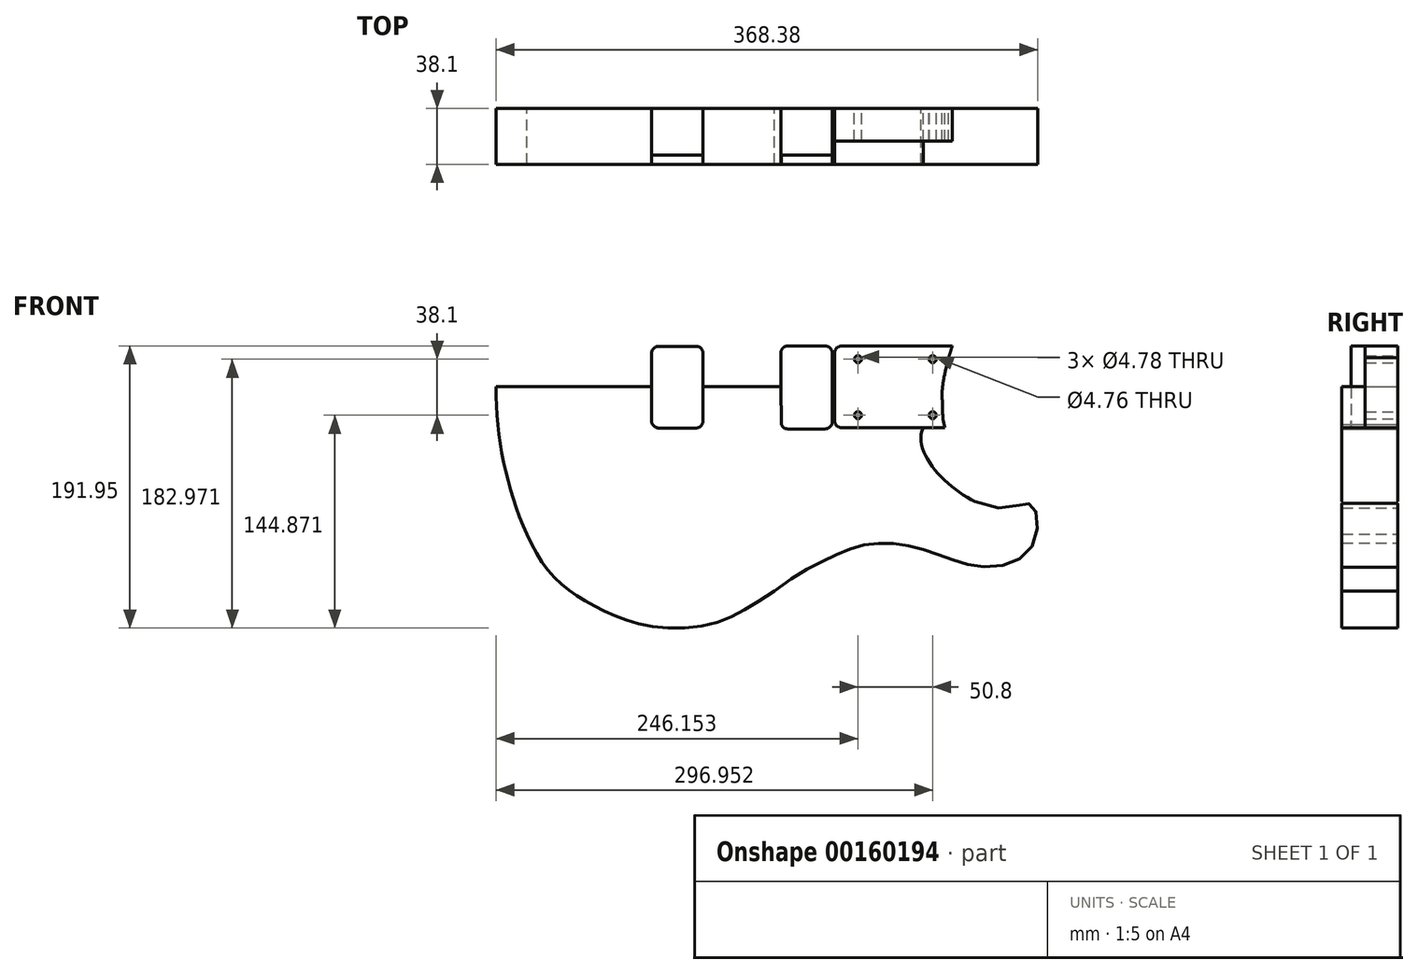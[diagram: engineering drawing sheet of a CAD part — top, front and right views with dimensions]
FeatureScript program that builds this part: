
annotation { "Feature Type Name" : "Feature", "Feature Type Description" : "" }
export const myFeature = defineFeature(function(context is Context, id is Id, definition is map)
    precondition{}
    {
        {
            var Q0;
            Q0=qCreatedBy(makeId("Front.planeOp"),FACE);
            var sketch = newSketch(context, id + "F0", { "sketchPlane" : qUnion([Q0])});
            skLineSegment(sketch, "E0", {"start": v(-152.4, 0) * mm, "end": v(0, 0) * mm});
            skLineSegment(sketch, "E1", {"start": v(0, 0) * mm, "end": v(196.6, 0) * mm});
            skLineSegment(sketch, "E2", {"start": v(0, 0) * mm, "end": v(0, 152.4) * mm});
            skLineSegment(sketch, "E3", {"start": v(0, 152.4) * mm, "end": v(0, 0) * mm});
            skLineSegment(sketch, "E4", {"start": v(0, -152.4) * mm, "end": v(0, 0) * mm});
            skArc(sketch, "E5", {"start": v(-152.4, 0) * mm, "mid": v(-147.19, 50.87) * mm, "end": v(-131.76, 99.62) * mm});
            skFitSpline(sketch, "E6", {"points": [v(-131.47, 100.28) * mm, v(-122.83, 116.5) * mm, v(-113.38, 128.92) * mm, v(-102.11, 138.7) * mm, v(-88.63, 147.5) * mm, v(-70.19, 156.24) * mm, v(-43.25, 163.54) * mm, v(0, 159.69) * mm, v(36.78, 138.89) * mm], "startDerivative": vector(69.4, 145.54) * mm, "endDerivative": vector(274.54, -170.13) * mm});
            skFitSpline(sketch, "E7.MirrorCS", {"points": [v(-131.47, -100.28) * mm, v(-122.83, -116.5) * mm, v(-113.38, -128.92) * mm, v(-102.11, -138.7) * mm, v(-88.63, -147.5) * mm, v(-70.19, -156.24) * mm, v(-43.25, -163.54) * mm, v(0, -159.69) * mm, v(36.78, -138.89) * mm], "startDerivative": vector(69.4, -145.54) * mm, "endDerivative": vector(274.54, 170.13) * mm});
            skArc(sketch, "E8.MirrorCS", {"start": v(-152.4, 0) * mm, "mid": v(-147.11, -51.22) * mm, "end": v(-131.47, -100.28) * mm});
            skFitSpline(sketch, "E9", {"points": [v(36.78, 138.89) * mm, v(67.95, 121.5) * mm, v(87.83, 113.04) * mm, v(111.91, 110) * mm, v(156.78, 116.96) * mm, v(185.7, 129.2) * mm, v(222.31, 130.72) * mm, v(254.22, 115.5) * mm, v(254.22, 101.8) * mm, v(230.67, 92.93) * mm, v(219.44, 89.3) * mm, v(196.97, 80.52) * mm, v(180.96, 68.45) * mm, v(169.25, 53.26) * mm, v(155.45, 19.68) * mm], "startDerivative": vector(277, -200.84) * mm, "endDerivative": vector(-90.45, -357.32) * mm});
            skLineSegment(sketch, "E10", {"start": v(115.94, 0) * mm, "end": v(115.94, 0) * mm});
            skFitSpline(sketch, "E11", {"points": [v(36.78, -138.89) * mm, v(71.72, -117.64) * mm, v(96.68, -107.92) * mm, v(122.28, -107.08) * mm, v(149.52, -114.5) * mm, v(178.54, -122.53) * mm, v(211.92, -108.98) * mm, v(211.92, -80.33) * mm, v(184.02, -81.68) * mm, v(138.89, -26.24) * mm], "startDerivative": vector(312.88, 253.05) * mm, "endDerivative": vector(219.64, 358.7) * mm});
            skLineSegment(sketch, "E12", {"start": v(77.88, 22.99) * mm, "end": v(77.88, -23.03) * mm});
            skPoint(sketch, "E13.visualSharp", {"position": v(76.95, 17.82) * mm});
            skArc(sketch, "E13.filletArc", {"start": v(82.65, 27.76) * mm, "mid": v(79.28, 26.36) * mm, "end": v(77.88, 22.99) * mm});
            skPoint(sketch, "E14.visualSharp", {"position": v(77.88, -37.74) * mm});
            skArc(sketch, "E14.filletArc", {"start": v(77.88, -23.03) * mm, "mid": v(79.28, -26.4) * mm, "end": v(82.65, -27.8) * mm});
            skCircle(sketch, "E15", {"center": v(144.55, -19.3) * mm, "radius": 2.39 * mm});
            skCircle(sketch, "E16", {"center": v(144.55, 18.8) * mm, "radius": 2.38 * mm});
            skCircle(sketch, "E17", {"center": v(93.75, 18.8) * mm, "radius": 2.39 * mm});
            skCircle(sketch, "E18", {"center": v(93.75, -19.3) * mm, "radius": 2.39 * mm});
            skArc(sketch, "E19.filletArc", {"start": v(-131.42, 100.38) * mm, "mid": v(-131.47, 100.28) * mm, "end": v(-131.51, 100.19) * mm});
            skArc(sketch, "E20.filletArc", {"start": v(-131.16, 100.93) * mm, "mid": v(-131.47, 100.28) * mm, "end": v(-131.76, 99.62) * mm});
            skLineSegment(sketch, "E21.bottom", {"start": v(71.48, 27.78) * mm, "end": v(46.08, 27.78) * mm});
            skLineSegment(sketch, "E22.bottom", {"start": v(-16.34, 27.56) * mm, "end": v(-41.74, 27.56) * mm});
            skLineSegment(sketch, "E22.top", {"start": v(-16.34, -28.01) * mm, "end": v(-41.74, -28.01) * mm});
            skLineSegment(sketch, "E22.left", {"start": v(-11.57, 22.79) * mm, "end": v(-11.57, -23.24) * mm});
            skLineSegment(sketch, "E22.right", {"start": v(-46.52, 22.79) * mm, "end": v(-46.52, -23.24) * mm});
            skPoint(sketch, "E23.visualSharp", {"position": v(-46.52, -28.01) * mm});
            skArc(sketch, "E23.filletArc", {"start": v(-46.52, -23.24) * mm, "mid": v(-45.12, -26.61) * mm, "end": v(-41.74, -28.01) * mm});
            skPoint(sketch, "E24.visualSharp", {"position": v(-11.57, -28.01) * mm});
            skArc(sketch, "E24.filletArc", {"start": v(-16.34, -28.01) * mm, "mid": v(-12.97, -26.61) * mm, "end": v(-11.57, -23.24) * mm});
            skPoint(sketch, "E25.visualSharp", {"position": v(-11.57, 27.56) * mm});
            skArc(sketch, "E25.filletArc", {"start": v(-11.57, 22.79) * mm, "mid": v(-12.97, 26.16) * mm, "end": v(-16.34, 27.56) * mm});
            skPoint(sketch, "E26.visualSharp", {"position": v(-46.52, 27.56) * mm});
            skArc(sketch, "E26.filletArc", {"start": v(-41.74, 27.56) * mm, "mid": v(-45.12, 26.16) * mm, "end": v(-46.52, 22.79) * mm});
            skPoint(sketch, "E27.visualSharp", {"position": v(56.16, -39.79) * mm});
            skArc(sketch, "E27.filletArc", {"start": v(71.48, -28.62) * mm, "mid": v(74.85, -27.22) * mm, "end": v(76.25, -23.85) * mm});
            skPoint(sketch, "E28.visualSharp", {"position": v(0, -39.79) * mm});
            skArc(sketch, "E28.filletArc", {"start": v(41.66, -25.66) * mm, "mid": v(43.42, -27.81) * mm, "end": v(46.08, -28.62) * mm});
            skPoint(sketch, "E29.visualSharp", {"position": v(-1.31, 27.78) * mm});
            skPoint(sketch, "E30.visualSharp", {"position": v(56.16, 27.78) * mm});
            skArc(sketch, "E30.filletArc", {"start": v(76.25, 23) * mm, "mid": v(74.85, 26.38) * mm, "end": v(71.48, 27.78) * mm});
            skPoint(sketch, "E31.visualSharp", {"position": v(152.77, -27.8) * mm});
            skPoint(sketch, "E32.visualSharp", {"position": v(21.17, 27.78) * mm});
            skArc(sketch, "E32.filletArc", {"start": v(46.08, 27.78) * mm, "mid": v(42.69, 26.37) * mm, "end": v(41.3, 22.97) * mm});
            skLineSegment(sketch, "E33", {"start": v(-152.4, 0) * mm, "end": v(253.29, 0) * mm});
            skFitSpline(sketch, "E34", {"points": [v(173.28, -77.9) * mm, v(158.7, -47.61) * mm, v(152.77, -27.8) * mm], "startDerivative": vector(-27.54, 20.36) * mm, "endDerivative": vector(-22.3, 77.16) * mm});
            skFitSpline(sketch, "E35", {"points": [v(152.77, -27.8) * mm, v(151.14, -10.76) * mm, v(155.45, 19.68) * mm], "startDerivative": vector(-12.52, 48.52) * mm, "endDerivative": vector(28.24, 103.09) * mm});
            skLineSegment(sketch, "E36", {"start": v(82.65, -27.8) * mm, "end": v(152.77, -27.8) * mm});
            skLineSegment(sketch, "E37", {"start": v(82.65, 27.76) * mm, "end": v(158.03, 27.76) * mm});
            skLineSegment(sketch, "E38", {"start": v(41.3, 22.97) * mm, "end": v(41.66, -25.66) * mm});
            skLineSegment(sketch, "E39", {"start": v(76.25, 23) * mm, "end": v(76.25, -23.85) * mm});
            skLineSegment(sketch, "E40", {"start": v(46.08, -28.62) * mm, "end": v(71.48, -28.62) * mm});
            skSolve(sketch);
        }
        {
            var Q0;
            {var subQ4=sQuery(id+"F0.wireOp",EDGE,"C4kIXPfx-N5O4-hiTY-XNcs-kao8R1ZWTTXV");Q0=makeQuery(id+"F0.imprint","IMPRINT",FACE,{"disambiguationData":[TD([[makeQuery(id+"F0.imprint","IMPRINT",EDGE,{"derivedFrom":subQ4}),-1.0]])]});}
            var Q1;
            {var subQ0=sQuery(id+"F0.wireOp",EDGE,"E8.MirrorCS");Q1=makeQuery(id+"F0.imprint","IMPRINT",FACE,{"disambiguationData":[TD([[makeQuery(id+"F0.imprint","IMPRINT",EDGE,{"derivedFrom":subQ0}),1.0]])]});}
            var Q2;
            {var subQ11=sQuery(id+"F0.wireOp",EDGE,"E5");Q2=makeQuery(id+"F0.imprint","IMPRINT",FACE,{"disambiguationData":[TD([[makeQuery(id+"F0.imprint","IMPRINT",EDGE,{"derivedFrom":subQ11}),-1.0]])]});}
            var Q3;
            {var subQ11=sQuery(id+"F0.wireOp",EDGE,"E11");Q3=makeQuery(id+"F0.imprint","IMPRINT",FACE,{"disambiguationData":[TD([[makeQuery(id+"F0.imprint","IMPRINT",EDGE,{"derivedFrom":subQ11}),1.0]])]});}
            extrude(context, id + "F1", {"entities" : qUnion([Q0, Q1, Q2, Q3]), "depth" : 38.1 * mm});
        }
        {
            var Q0;
            Q0=makeQuery(id+"F0.imprint","IMPRINT",FACE,{"disambiguationData":[TD([[makeQuery(id+"F0.imprint","IMPRINT",EDGE,{"derivedFrom":sQuery(id+"F0.wireOp",EDGE,"E22.bottom")}),1.0]])]});
            var Q1;
            Q1=makeQuery(id+"F0.imprint","IMPRINT",FACE,{"disambiguationData":[TD([[makeQuery(id+"F0.imprint","IMPRINT",EDGE,{"derivedFrom":sQuery(id+"F0.wireOp",EDGE,"E22.top")}),-1.0]])]});
            var Q2;
            Q2=makeQuery(id+"F0.imprint","IMPRINT",FACE,{"disambiguationData":[TD([[makeQuery(id+"F0.imprint","IMPRINT",EDGE,{"derivedFrom":sQuery(id+"F0.wireOp",EDGE,"E21.bottom")}),1.0]])]});
            var Q3;
            {var subQ6=sQuery(id+"F0.wireOp",EDGE,"E27.filletArc");Q3=makeQuery(id+"F0.imprint","IMPRINT",FACE,{"disambiguationData":[TD([[makeQuery(id+"F0.imprint","IMPRINT",EDGE,{"derivedFrom":subQ6}),1.0]])]});}
            var Q4;
            Q4=sQuery(id+"F0.wireOp",EDGE,"E22.bottom");
            var Q5;
            Q5=sQuery(id+"F0.wireOp",EDGE,"E22.left");
            var Q6;
            Q6=sQuery(id+"F0.wireOp",EDGE,"E22.right");
            var Q7;
            Q7=sQuery(id+"F0.wireOp",EDGE,"E21.left");
            var Q8;
            Q8=sQuery(id+"F0.wireOp",EDGE,"wgNcPVM6-9Sos-h06Y-WuoE-GcpxYMtAUpaX");
            var Q9;
            Q9=sQuery(id+"F0.wireOp",EDGE,"E21.bottom");
            var Q10;
            Q10=sQuery(id+"F0.wireOp",EDGE,"E21.top");
            var Q11;
            Q11=sQuery(id+"F0.wireOp",EDGE,"E22.top");
            extrude(context, id + "F2", {"entities" : qUnion([Q0, Q1, Q2, Q3]), "surfaceEntities" : qUnion([Q4, Q5, Q6, Q7, Q8, Q9, Q10, Q11]), "depth" : 31.75 * mm});
        }
        {
            var Q0;
            {var subQ0=sQuery(id+"F0.wireOp",EDGE,"E13.filletArc");Q0=makeQuery(id+"F0.imprint","IMPRINT",FACE,{"disambiguationData":[TD([[makeQuery(id+"F0.imprint","IMPRINT",EDGE,{"derivedFrom":subQ0}),1.0]])]});}
            var Q1;
            {var subQ4=sQuery(id+"F0.wireOp",EDGE,"E14.filletArc");Q1=makeQuery(id+"F0.imprint","IMPRINT",FACE,{"disambiguationData":[TD([[makeQuery(id+"F0.imprint","IMPRINT",EDGE,{"derivedFrom":subQ4}),1.0]])]});}
            extrude(context, id + "F3", {"entities" : qUnion([Q0, Q1]), "operationType" : NewBodyOperationType.ADD, "depth" : 22.22 * mm});
        }
    });
